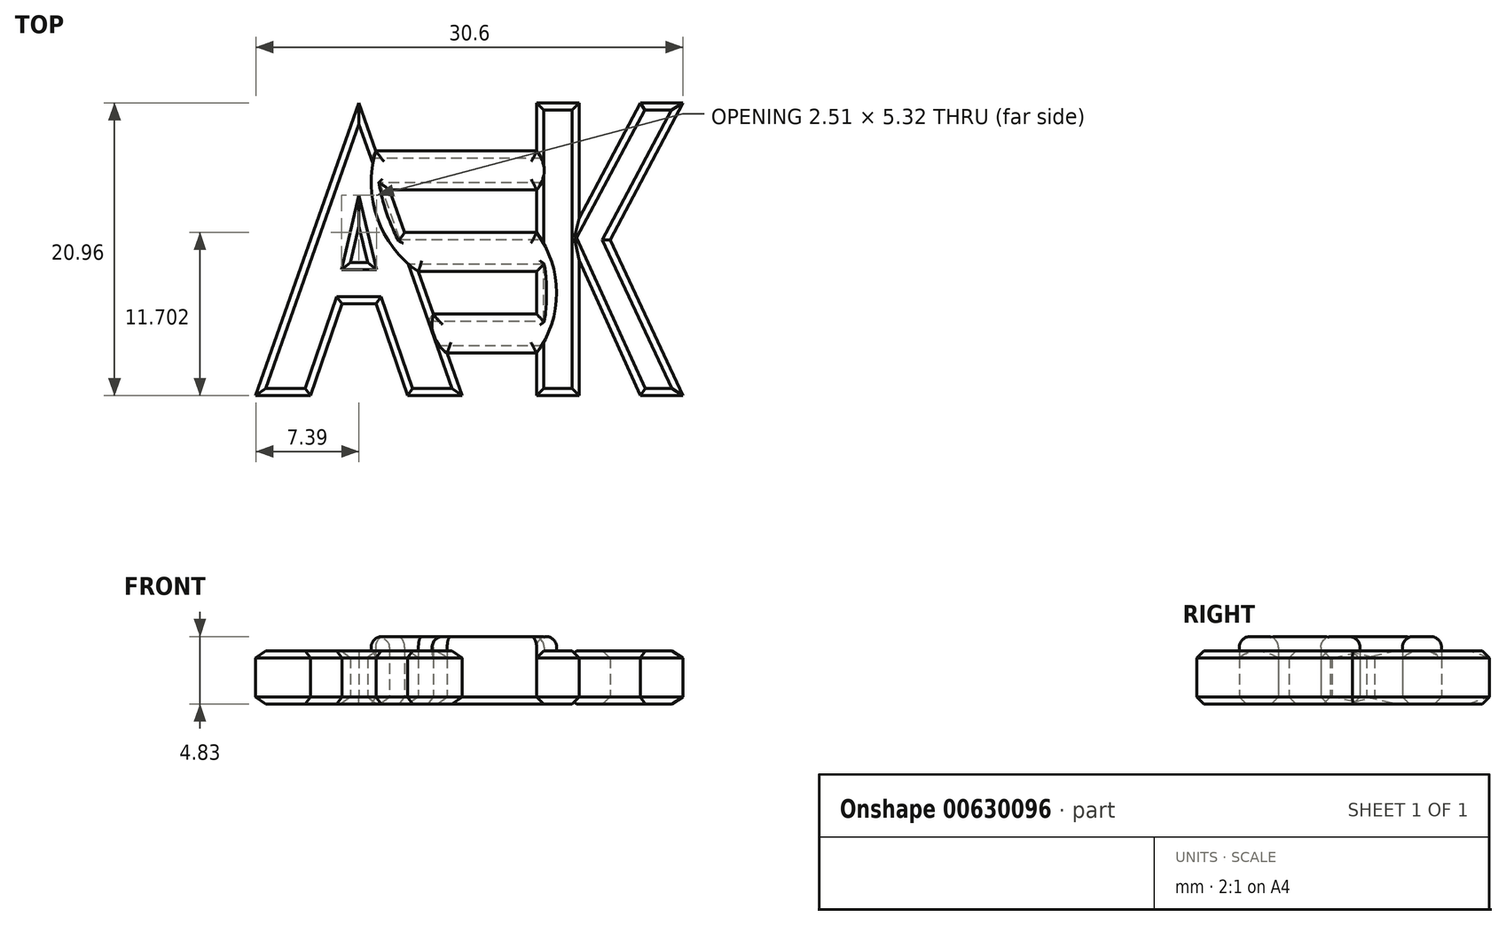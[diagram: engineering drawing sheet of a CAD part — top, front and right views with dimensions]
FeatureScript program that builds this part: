
annotation { "Feature Type Name" : "Feature", "Feature Type Description" : "" }
export const myFeature = defineFeature(function(context is Context, id is Id, definition is map)
    precondition{}
    {
        {
            var Q0;
            Q0=qCreatedBy(makeId("Top.planeOp"),FACE);
            var sketch = newSketch(context, id + "F0", { "sketchPlane" : qUnion([Q0])});
            skLineSegment(sketch, "E0", {"start": v(0, 69.63) * mm, "end": v(0, -56.44) * mm});
            skLineSegment(sketch, "E1", {"start": v(0, 20.96) * mm, "end": v(-7.4, 0) * mm});
            skLineSegment(sketch, "E2", {"start": v(-7.4, 0) * mm, "end": v(-3.48, 0) * mm});
            skLineSegment(sketch, "E3", {"start": v(-3.48, 0) * mm, "end": v(-1.23, 6.6) * mm});
            skPoint(sketch, "E3.endSnap0", {"position": v(0, 6.6) * mm});
            skLineSegment(sketch, "E4", {"start": v(-1.23, 6.6) * mm, "end": v(0, 6.6) * mm});
            skLineSegment(sketch, "E5.MirrorCS", {"start": v(0, 20.96) * mm, "end": v(1.21, 17.52) * mm});
            skLineSegment(sketch, "E6.MirrorCS", {"start": v(7.4, 0) * mm, "end": v(3.48, 0) * mm});
            skLineSegment(sketch, "E7.MirrorCS", {"start": v(3.48, 0) * mm, "end": v(1.23, 6.6) * mm});
            skLineSegment(sketch, "E8.MirrorCS", {"start": v(1.23, 6.6) * mm, "end": v(0, 6.6) * mm});
            skLineSegment(sketch, "E9", {"start": v(-0.61, 9.55) * mm, "end": v(0, 9.55) * mm});
            skPoint(sketch, "E9.startSnap0", {"position": v(-0.61, 6.6) * mm});
            skLineSegment(sketch, "E10", {"start": v(-0.61, 9.55) * mm, "end": v(0, 12.15) * mm});
            skLineSegment(sketch, "E11.MirrorCS", {"start": v(0.61, 9.55) * mm, "end": v(0, 12.15) * mm});
            skLineSegment(sketch, "E12.MirrorCS", {"start": v(0.61, 9.55) * mm, "end": v(0, 9.55) * mm});
            skLineSegment(sketch, "E13", {"start": v(6.32, 3.04) * mm, "end": v(12.72, 3.04) * mm});
            skLineSegment(sketch, "E14", {"start": v(5.33, 5.84) * mm, "end": v(12.72, 5.84) * mm});
            skLineSegment(sketch, "E15", {"start": v(4.26, 8.89) * mm, "end": v(12.72, 8.89) * mm});
            skLineSegment(sketch, "E16", {"start": v(3.27, 11.68) * mm, "end": v(12.72, 11.68) * mm});
            skLineSegment(sketch, "E17", {"start": v(2.2, 14.73) * mm, "end": v(12.72, 14.73) * mm});
            skLineSegment(sketch, "E18", {"start": v(1.21, 17.52) * mm, "end": v(12.72, 17.52) * mm});
            skLineSegment(sketch, "E19", {"start": v(12.72, 20.96) * mm, "end": v(12.72, 17.52) * mm});
            skLineSegment(sketch, "E20", {"start": v(12.72, 0) * mm, "end": v(15.77, 0) * mm});
            skLineSegment(sketch, "E21", {"start": v(15.77, 0) * mm, "end": v(15.77, 9.69) * mm});
            skLineSegment(sketch, "E22", {"start": v(15.77, 9.69) * mm, "end": v(20.16, 0) * mm});
            skLineSegment(sketch, "E23", {"start": v(20.16, 0) * mm, "end": v(23.2, 0) * mm});
            skLineSegment(sketch, "E24", {"start": v(12.72, 20.96) * mm, "end": v(15.77, 20.96) * mm});
            skLineSegment(sketch, "E25", {"start": v(15.77, 20.96) * mm, "end": v(15.77, 12.72) * mm});
            skLineSegment(sketch, "E26", {"start": v(15.77, 12.72) * mm, "end": v(20.16, 20.96) * mm});
            skLineSegment(sketch, "E27", {"start": v(20.16, 20.96) * mm, "end": v(23.2, 20.96) * mm});
            skLineSegment(sketch, "E28", {"start": v(23.2, 0) * mm, "end": v(17.99, 11.15) * mm});
            skLineSegment(sketch, "E29", {"start": v(17.99, 11.15) * mm, "end": v(23.2, 20.96) * mm});
            skLineSegment(sketch, "E30.trimOffspring", {"start": v(2.2, 14.73) * mm, "end": v(3.27, 11.68) * mm});
            skLineSegment(sketch, "E31.trimOffspring", {"start": v(12.72, 14.73) * mm, "end": v(12.72, 5.84) * mm});
            skLineSegment(sketch, "E32.trimOffspring", {"start": v(4.26, 8.89) * mm, "end": v(5.33, 5.84) * mm});
            skLineSegment(sketch, "E33.trimOffspring", {"start": v(6.32, 3.04) * mm, "end": v(7.4, 0) * mm});
            skLineSegment(sketch, "E34.trimOffspring", {"start": v(12.72, 3.04) * mm, "end": v(12.72, 0) * mm});
            skArc(sketch, "E35", {"start": v(1.21, 17.52) * mm, "mid": v(1.35, 12.71) * mm, "end": v(4.26, 8.89) * mm});
            skArc(sketch, "E36", {"start": v(12.72, 3.04) * mm, "mid": v(13.9, 7.36) * mm, "end": v(12.72, 11.68) * mm});
            skArc(sketch, "E37", {"start": v(12.72, 14.73) * mm, "mid": v(13.18, 16.12) * mm, "end": v(12.72, 17.52) * mm});
            skArc(sketch, "E38", {"start": v(5.33, 5.84) * mm, "mid": v(5.24, 4.23) * mm, "end": v(6.32, 3.04) * mm});
            skSolve(sketch);
        }
        {
            var Q0;
            Q0 = qSketchRegion(id + "F0", true);
            extrude(context, id + "F1", {"entities" : qUnion([Q0]), "depth" : 3.8 * mm, "offsetDistance" : 25.4 * mm});
        }
        {
            var Q0;
            Q0=makeQuery(id+"F1.opExtrude","CAP_FACE",FACE,{"disambiguationData":[OSD([sQuery(id+"F0.wireOp",EDGE,"E1"),sQuery(id+"F0.wireOp",EDGE,"E2"),sQuery(id+"F0.wireOp",EDGE,"E3"),sQuery(id+"F0.wireOp",EDGE,"E4"),sQuery(id+"F0.wireOp",EDGE,"E5.MirrorCS"),sQuery(id+"F0.wireOp",EDGE,"E6.MirrorCS"),sQuery(id+"F0.wireOp",EDGE,"E7.MirrorCS"),sQuery(id+"F0.wireOp",EDGE,"E8.MirrorCS"),sQuery(id+"F0.wireOp",EDGE,"E9"),sQuery(id+"F0.wireOp",EDGE,"E10"),sQuery(id+"F0.wireOp",EDGE,"E11.MirrorCS"),sQuery(id+"F0.wireOp",EDGE,"E12.MirrorCS"),sQuery(id+"F0.wireOp",EDGE,"E13"),sQuery(id+"F0.wireOp",EDGE,"E14"),sQuery(id+"F0.wireOp",EDGE,"E15"),sQuery(id+"F0.wireOp",EDGE,"E16"),sQuery(id+"F0.wireOp",EDGE,"E17"),sQuery(id+"F0.wireOp",EDGE,"E18"),sQuery(id+"F0.wireOp",EDGE,"E19"),sQuery(id+"F0.wireOp",EDGE,"E20"),sQuery(id+"F0.wireOp",EDGE,"E21"),sQuery(id+"F0.wireOp",EDGE,"E22"),sQuery(id+"F0.wireOp",EDGE,"E23"),sQuery(id+"F0.wireOp",EDGE,"E24"),sQuery(id+"F0.wireOp",EDGE,"E25"),sQuery(id+"F0.wireOp",EDGE,"E26"),sQuery(id+"F0.wireOp",EDGE,"E27"),sQuery(id+"F0.wireOp",EDGE,"E28"),sQuery(id+"F0.wireOp",EDGE,"E29"),sQuery(id+"F0.wireOp",EDGE,"E30.trimOffspring"),sQuery(id+"F0.wireOp",EDGE,"E31.trimOffspring"),sQuery(id+"F0.wireOp",EDGE,"E32.trimOffspring"),sQuery(id+"F0.wireOp",EDGE,"E33.trimOffspring"),sQuery(id+"F0.wireOp",EDGE,"E34.trimOffspring")])],"isStart":false});
            var sketch = newSketch(context, id + "F2", { "sketchPlane" : qUnion([Q0])});
            skArc(sketch, "E39", {"start": v(1.21, 17.52) * mm, "mid": v(1.32, 12.7) * mm, "end": v(4.26, 8.89) * mm});
            skArc(sketch, "E40", {"start": v(12.72, 14.73) * mm, "mid": v(13.26, 16.12) * mm, "end": v(12.72, 17.52) * mm});
            skArc(sketch, "E41", {"start": v(12.72, 3.04) * mm, "mid": v(14.15, 7.36) * mm, "end": v(12.72, 11.68) * mm});
            skArc(sketch, "E42", {"start": v(5.33, 5.84) * mm, "mid": v(5.38, 4.28) * mm, "end": v(6.32, 3.04) * mm});
            skSolve(sketch);
        }
        {
            var Q0;
            Q0 = qSketchRegion(id + "F2", true);
            var Q1;
            Q1=makeQuery(id+"F2.imprint","IMPRINT",FACE,{"disambiguationData":[TD([[makeQuery(id+"F2.imprint","IMPRINT",EDGE,{"derivedFrom":sQuery(id+"F2.wireOp",EDGE,"E39")}),1.0]])]});
            extrude(context, id + "F3", {"entities" : qUnion([Q0, Q1]), "operationType" : NewBodyOperationType.ADD, "depth" : 1.02 * mm, "offsetDistance" : 25.4 * mm});
        }
        {
            var Q0;
            Q0=makeQuery(id+"F3.opExtrude","CAP_FACE",FACE,{"disambiguationData":[OSD([sQuery(id+"F0.wireOp",EDGE,"E13"),sQuery(id+"F0.wireOp",EDGE,"E14"),sQuery(id+"F0.wireOp",EDGE,"E15"),sQuery(id+"F0.wireOp",EDGE,"E16"),sQuery(id+"F0.wireOp",EDGE,"E17"),sQuery(id+"F0.wireOp",EDGE,"E18"),sQuery(id+"F0.wireOp",EDGE,"E30.trimOffspring"),sQuery(id+"F0.wireOp",EDGE,"E31.trimOffspring"),sQuery(id+"F2.wireOp",EDGE,"E39"),sQuery(id+"F2.wireOp",EDGE,"E40"),sQuery(id+"F2.wireOp",EDGE,"E41"),sQuery(id+"F2.wireOp",EDGE,"E42")])],"isStart":false});
            fillet(context, id + "F4", {"entities" : qUnion([Q0]), "radius" : 0.76 * mm, "tangentPropagation" : true, "allowEdgeOverflow" : false});
        }
        {
            var Q0;
            Q0=makeQuery(id+"F1.opExtrude","CAP_EDGE",EDGE,{"disambiguationData":[OSD([sQuery(id+"F0.wireOp",EDGE,"E1")])],"isStart":false});
            var Q1;
            Q1=makeQuery(id+"F1.opExtrude","CAP_EDGE",EDGE,{"disambiguationData":[OSD([sQuery(id+"F0.wireOp",EDGE,"E2")])],"isStart":false});
            var Q2;
            Q2=makeQuery(id+"F1.opExtrude","CAP_EDGE",EDGE,{"disambiguationData":[OSD([sQuery(id+"F0.wireOp",EDGE,"E3")])],"isStart":false});
            var Q3;
            Q3=makeQuery(id+"F1.opExtrude","CAP_EDGE",EDGE,{"disambiguationData":[OSD([sQuery(id+"F0.wireOp",EDGE,"E4"),sQuery(id+"F0.wireOp",EDGE,"E8.MirrorCS")])],"isStart":false});
            var Q4;
            Q4=makeQuery(id+"F1.opExtrude","CAP_EDGE",EDGE,{"disambiguationData":[OSD([sQuery(id+"F0.wireOp",EDGE,"E7.MirrorCS")])],"isStart":false});
            var Q5;
            Q5=makeQuery(id+"F1.opExtrude","CAP_EDGE",EDGE,{"disambiguationData":[OSD([sQuery(id+"F0.wireOp",EDGE,"E6.MirrorCS")])],"isStart":false});
            var Q6;
            Q6=makeQuery(id+"F1.opExtrude","CAP_EDGE",EDGE,{"disambiguationData":[OSD([sQuery(id+"F0.wireOp",EDGE,"E33.trimOffspring")])],"isStart":false});
            var Q7;
            Q7=makeQuery(id+"F1.opExtrude","CAP_EDGE",EDGE,{"disambiguationData":[OSD([sQuery(id+"F0.wireOp",EDGE,"E5.MirrorCS")])],"isStart":false});
            var Q8;
            Q8=makeQuery(id+"F1.opExtrude","CAP_EDGE",EDGE,{"disambiguationData":[OSD([sQuery(id+"F0.wireOp",EDGE,"E10")])],"isStart":false});
            var Q9;
            Q9=makeQuery(id+"F1.opExtrude","CAP_EDGE",EDGE,{"disambiguationData":[OSD([sQuery(id+"F0.wireOp",EDGE,"E11.MirrorCS")])],"isStart":false});
            var Q10;
            Q10=makeQuery(id+"F1.opExtrude","CAP_EDGE",EDGE,{"disambiguationData":[OSD([sQuery(id+"F0.wireOp",EDGE,"E9"),sQuery(id+"F0.wireOp",EDGE,"E12.MirrorCS")])],"isStart":false});
            var Q11;
            Q11=makeQuery(id+"F1.opExtrude","CAP_EDGE",EDGE,{"disambiguationData":[OSD([sQuery(id+"F0.wireOp",EDGE,"E34.trimOffspring")])],"isStart":false});
            var Q12;
            Q12=makeQuery(id+"F1.opExtrude","CAP_EDGE",EDGE,{"disambiguationData":[OSD([sQuery(id+"F0.wireOp",EDGE,"E21")])],"isStart":false});
            var Q13;
            Q13=makeQuery(id+"F1.opExtrude","CAP_EDGE",EDGE,{"disambiguationData":[OSD([sQuery(id+"F0.wireOp",EDGE,"E20")])],"isStart":false});
            var Q14;
            Q14=makeQuery(id+"F1.opExtrude","CAP_EDGE",EDGE,{"disambiguationData":[OSD([sQuery(id+"F0.wireOp",EDGE,"E22")])],"isStart":false});
            var Q15;
            Q15=makeQuery(id+"F1.opExtrude","CAP_EDGE",EDGE,{"disambiguationData":[OSD([sQuery(id+"F0.wireOp",EDGE,"E23")])],"isStart":false});
            var Q16;
            Q16=makeQuery(id+"F1.opExtrude","CAP_EDGE",EDGE,{"disambiguationData":[OSD([sQuery(id+"F0.wireOp",EDGE,"E28")])],"isStart":false});
            var Q17;
            Q17=makeQuery(id+"F1.opExtrude","CAP_EDGE",EDGE,{"disambiguationData":[OSD([sQuery(id+"F0.wireOp",EDGE,"E29")])],"isStart":false});
            var Q18;
            Q18=makeQuery(id+"F1.opExtrude","CAP_EDGE",EDGE,{"disambiguationData":[OSD([sQuery(id+"F0.wireOp",EDGE,"E27")])],"isStart":false});
            var Q19;
            Q19=makeQuery(id+"F1.opExtrude","CAP_EDGE",EDGE,{"disambiguationData":[OSD([sQuery(id+"F0.wireOp",EDGE,"E26")])],"isStart":false});
            var Q20;
            Q20=makeQuery(id+"F1.opExtrude","CAP_EDGE",EDGE,{"disambiguationData":[OSD([sQuery(id+"F0.wireOp",EDGE,"E25")])],"isStart":false});
            var Q21;
            Q21=makeQuery(id+"F1.opExtrude","CAP_EDGE",EDGE,{"disambiguationData":[OSD([sQuery(id+"F0.wireOp",EDGE,"E24")])],"isStart":false});
            var Q22;
            Q22=makeQuery(id+"F1.opExtrude","CAP_EDGE",EDGE,{"disambiguationData":[OSD([sQuery(id+"F0.wireOp",EDGE,"E19")])],"isStart":false});
            var Q23;
            {var subQ0=sQuery(id+"F0.wireOp",EDGE,"E31.trimOffspring");Q23=makeQuery(id+"F1.opExtrude","CAP_EDGE",EDGE,{"disambiguationData":[OSD([subQ0]),TDD([makeQuery(id+"F0.imprint","IMPRINT",EDGE,{"disambiguationData":[TD([[makeQuery(id+"F0.imprint","INTERSECT",VERTEX,{"derivedFrom":[sQuery(id+"F0.wireOp",EDGE,"E16"),subQ0,sQuery(id+"F0.wireOp",EDGE,"E36")]}),1.0]])],"derivedFrom":subQ0})])],"isStart":false});}
            chamfer(context, id + "F5", {"entities" : qUnion([Q0, Q1, Q2, Q3, Q4, Q5, Q6, Q7, Q8, Q9, Q10, Q11, Q12, Q13, Q14, Q15, Q16, Q17, Q18, Q19, Q20, Q21, Q22, Q23]), "width" : 0.5 * mm, "tangentPropagation" : true});
        }
        {
            var Q0;
            Q0=makeQuery(id+"F1.opExtrude","CAP_FACE",FACE,{"disambiguationData":[OSD([sQuery(id+"F0.wireOp",EDGE,"E1"),sQuery(id+"F0.wireOp",EDGE,"E2"),sQuery(id+"F0.wireOp",EDGE,"E3"),sQuery(id+"F0.wireOp",EDGE,"E4"),sQuery(id+"F0.wireOp",EDGE,"E5.MirrorCS"),sQuery(id+"F0.wireOp",EDGE,"E6.MirrorCS"),sQuery(id+"F0.wireOp",EDGE,"E7.MirrorCS"),sQuery(id+"F0.wireOp",EDGE,"E8.MirrorCS"),sQuery(id+"F0.wireOp",EDGE,"E9"),sQuery(id+"F0.wireOp",EDGE,"E10"),sQuery(id+"F0.wireOp",EDGE,"E11.MirrorCS"),sQuery(id+"F0.wireOp",EDGE,"E12.MirrorCS"),sQuery(id+"F0.wireOp",EDGE,"E13"),sQuery(id+"F0.wireOp",EDGE,"E14"),sQuery(id+"F0.wireOp",EDGE,"E15"),sQuery(id+"F0.wireOp",EDGE,"E16"),sQuery(id+"F0.wireOp",EDGE,"E17"),sQuery(id+"F0.wireOp",EDGE,"E18"),sQuery(id+"F0.wireOp",EDGE,"E19"),sQuery(id+"F0.wireOp",EDGE,"E20"),sQuery(id+"F0.wireOp",EDGE,"E21"),sQuery(id+"F0.wireOp",EDGE,"E22"),sQuery(id+"F0.wireOp",EDGE,"E23"),sQuery(id+"F0.wireOp",EDGE,"E24"),sQuery(id+"F0.wireOp",EDGE,"E25"),sQuery(id+"F0.wireOp",EDGE,"E26"),sQuery(id+"F0.wireOp",EDGE,"E27"),sQuery(id+"F0.wireOp",EDGE,"E28"),sQuery(id+"F0.wireOp",EDGE,"E29"),sQuery(id+"F0.wireOp",EDGE,"E30.trimOffspring"),sQuery(id+"F0.wireOp",EDGE,"E31.trimOffspring"),sQuery(id+"F0.wireOp",EDGE,"E32.trimOffspring"),sQuery(id+"F0.wireOp",EDGE,"E33.trimOffspring"),sQuery(id+"F0.wireOp",EDGE,"E34.trimOffspring")])],"isStart":true});
            chamfer(context, id + "F6", {"entities" : qUnion([Q0]), "width" : 0.5 * mm, "tangentPropagation" : true});
        }
    });
